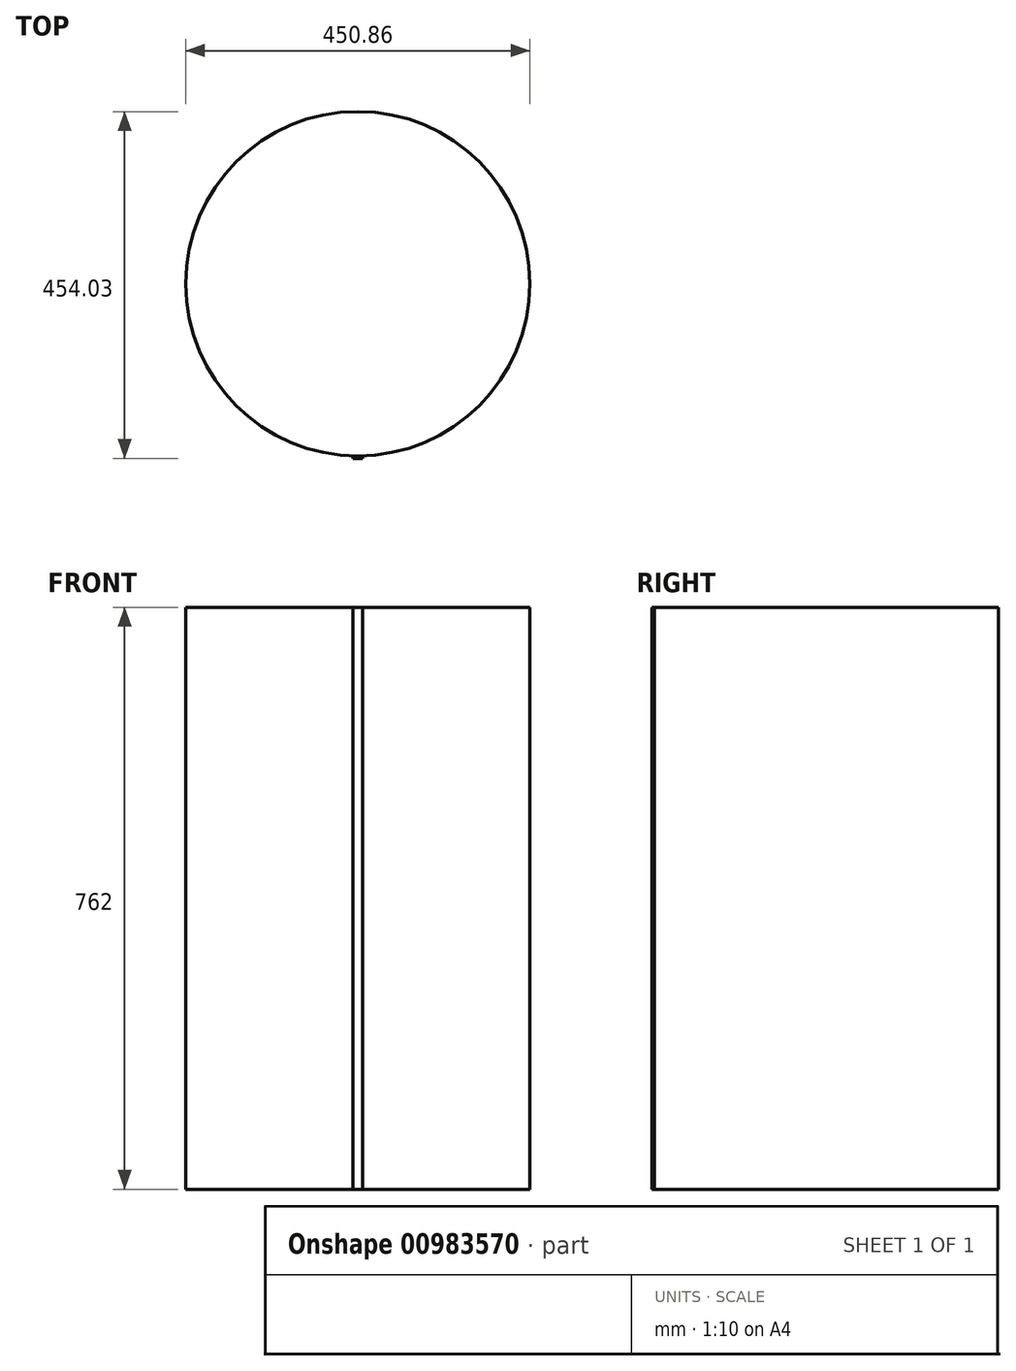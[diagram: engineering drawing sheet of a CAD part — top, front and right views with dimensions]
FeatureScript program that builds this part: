
annotation { "Feature Type Name" : "Feature", "Feature Type Description" : "" }
export const myFeature = defineFeature(function(context is Context, id is Id, definition is map)
    precondition{}
    {
        {
            var Q0;
            Q0=qCreatedBy(makeId("Top.planeOp"),FACE);
            var sketch = newSketch(context, id + "F0", { "sketchPlane" : qUnion([Q0])});
            skCircle(sketch, "E0", {"center": v(0, 0) * mm, "radius": 225.43 * mm});
            skSolve(sketch);
        }
        {
            var Q0;
            Q0 = qSketchRegion(id + "F0", true);
            extrude(context, id + "F1", {"entities" : qUnion([Q0]), "depth" : 762 * mm, "offsetDistance" : 25.4 * mm});
        }
        {
            var Q0;
            Q0=makeQuery(id+"F1.opExtrude","CAP_FACE",FACE,{"disambiguationData":[OSD([sQuery(id+"F0.wireOp",EDGE,"E0")])],"isStart":false});
            var sketch = newSketch(context, id + "F2", { "sketchPlane" : qUnion([Q0])});
            skLineSegment(sketch, "E1.bottom", {"start": v(-6.35, -226.06) * mm, "end": v(6.35, -226.06) * mm});
            skLineSegment(sketch, "E1.top", {"start": v(-6.35, -228.6) * mm, "end": v(6.35, -228.6) * mm});
            skLineSegment(sketch, "E1.left", {"start": v(-6.35, -226.06) * mm, "end": v(-6.35, -228.6) * mm});
            skLineSegment(sketch, "E1.right", {"start": v(6.35, -226.06) * mm, "end": v(6.35, -228.6) * mm});
            skSolve(sketch);
        }
        {
            var Q0;
            Q0=makeQuery(id+"F2.imprint","IMPRINT",FACE,{"disambiguationData":[TD([[makeQuery(id+"F2.imprint","IMPRINT",EDGE,{"derivedFrom":sQuery(id+"F2.wireOp",EDGE,"E1.top")}),1.0]])]});
            extrude(context, id + "F3", {"entities" : qUnion([Q0]), "operationType" : NewBodyOperationType.ADD, "oppositeDirection" : true, "depth" : 762 * mm, "offsetDistance" : 25.4 * mm});
        }
    });
